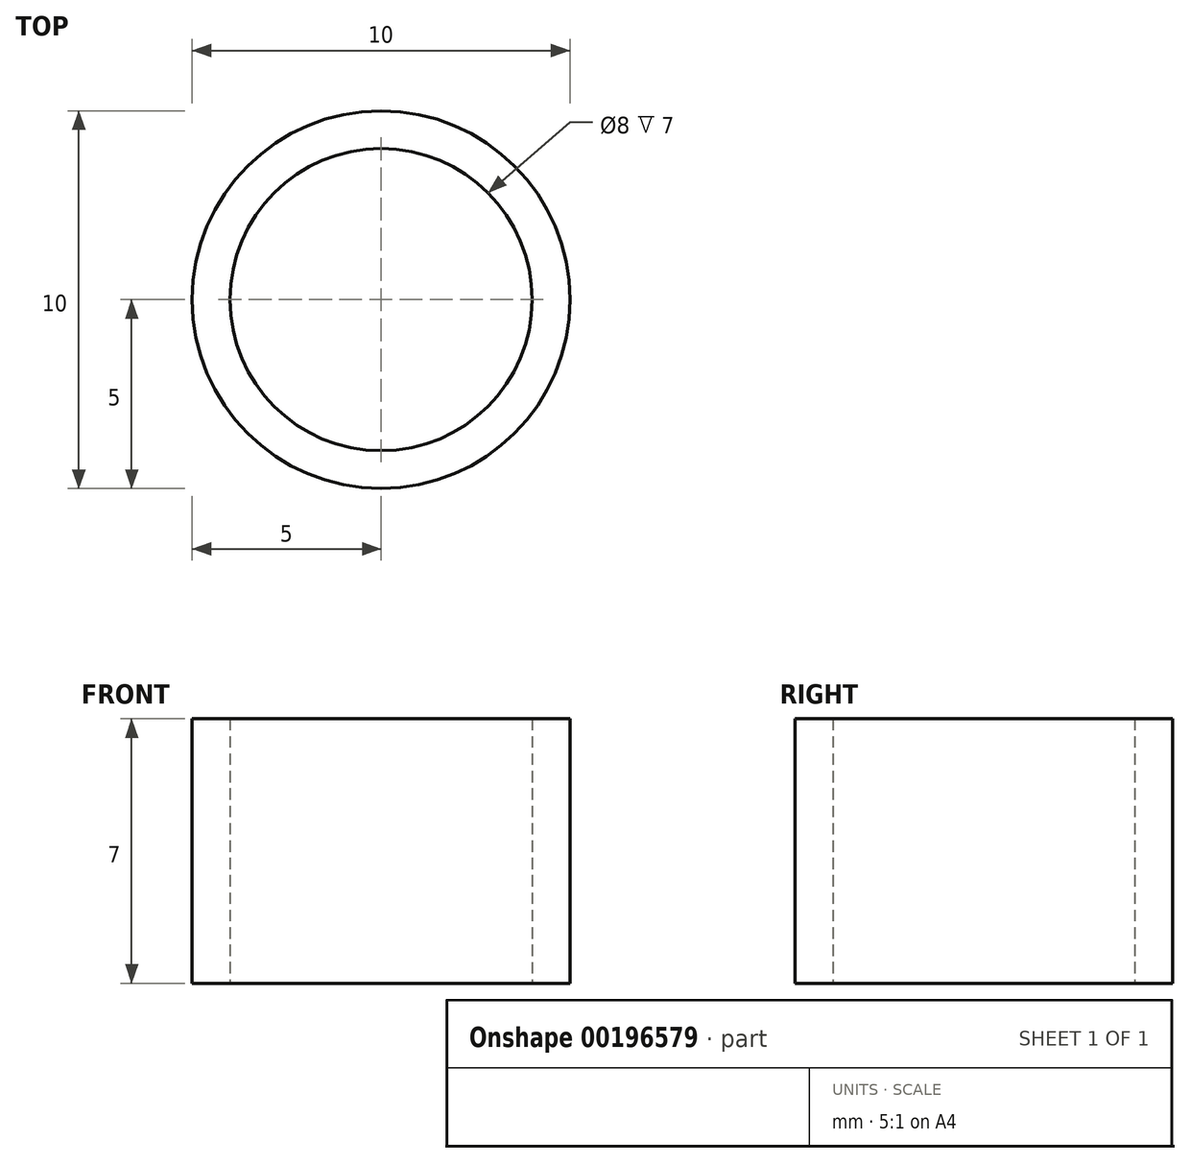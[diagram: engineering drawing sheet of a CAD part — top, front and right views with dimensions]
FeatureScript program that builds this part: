
annotation { "Feature Type Name" : "Feature", "Feature Type Description" : "" }
export const myFeature = defineFeature(function(context is Context, id is Id, definition is map)
    precondition{}
    {
        {
            var Q0;
            Q0=qCreatedBy(makeId("Top.planeOp"),FACE);
            var sketch = newSketch(context, id + "F0", { "sketchPlane" : qUnion([Q0])});
            skCircle(sketch, "E0", {"center": v(0, 0) * mm, "radius": 5 * mm});
            skCircle(sketch, "E1", {"center": v(0, 0) * mm, "radius": 4 * mm});
            skSolve(sketch);
        }
        {
            var Q0;
            Q0 = qSketchRegion(id + "F0", true);
            extrude(context, id + "F1", {"entities" : qUnion([Q0]), "depth" : 7 * mm});
        }
    });
